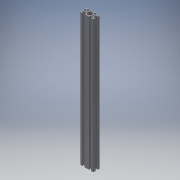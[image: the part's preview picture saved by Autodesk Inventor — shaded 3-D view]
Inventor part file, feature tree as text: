
AUTODESK INVENTOR PART (.ipt)
format: ipt  version: 2018 (Build 220112000, 112)  size: 344,576 bytes
history: native  units: mm
features: extrude x1, sketch x1, projected_geometry x1, imported_body x1
ambient origin geometry x8: Origin, YZ Plane, XZ Plane, XY Plane, X Axis, Y Axis, Z Axis, Center Point
bodies: Solid1 (feature_tree)
feature tree (4):
  extrude  "Extrusion1"  [1 undecoded]
  sketch  "Sketch1"  dims[d0=650.0mm d1=0.0mm]
  projected_geometry  "Projected Loop1"
  imported_body  "Base1"
note: 1 required parameter value undecoded (feature->parameter linkage not recoverable at this tier; creation-order binding heuristic only, values carry confidence <= 0.55)
